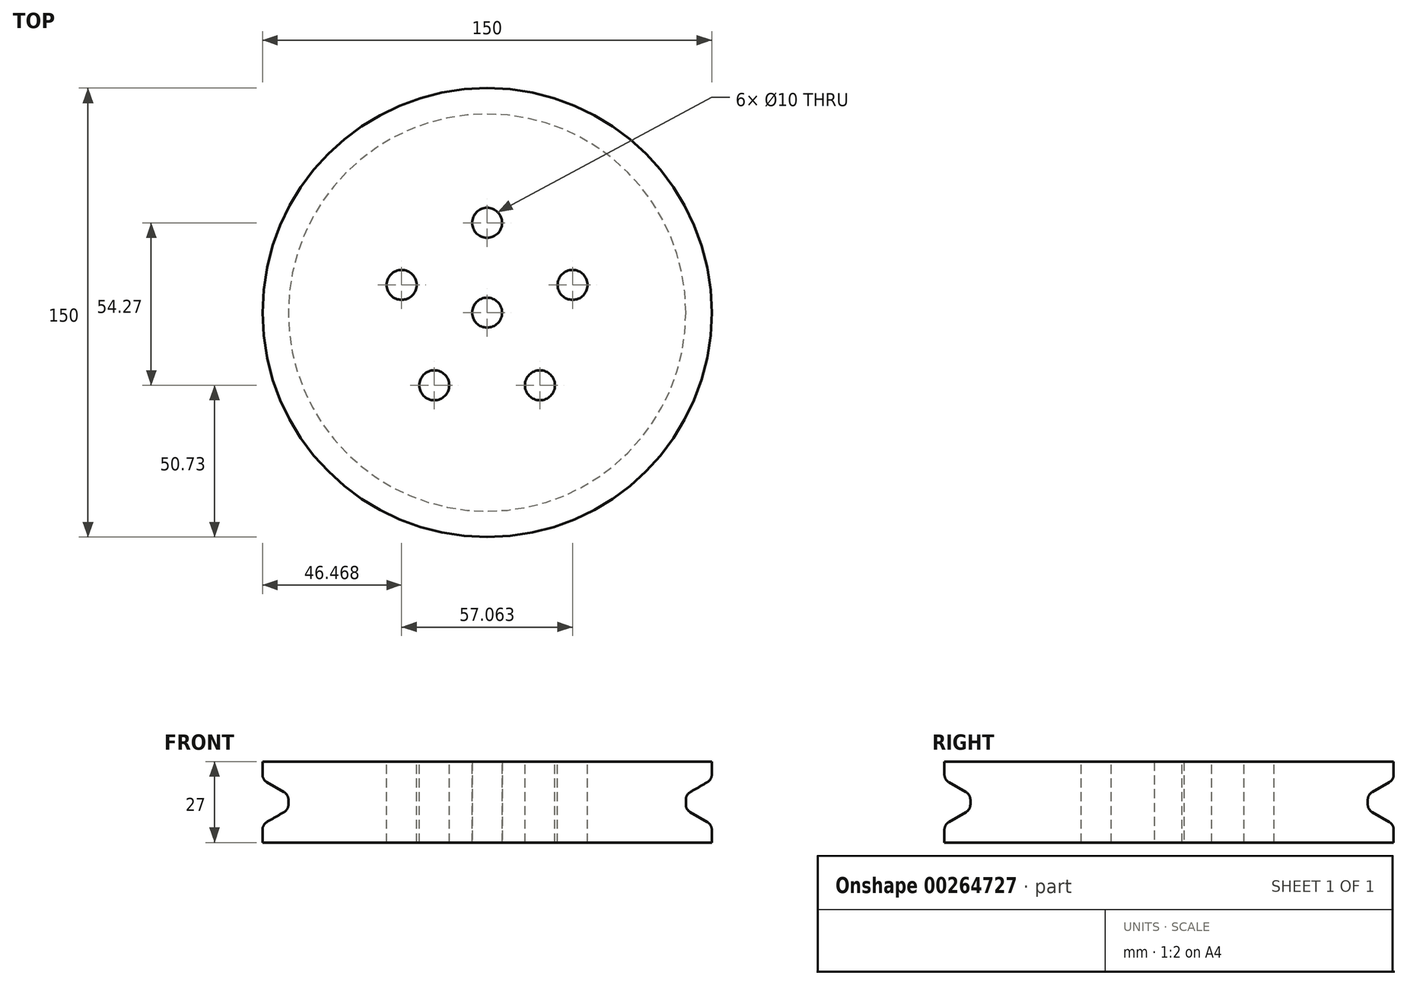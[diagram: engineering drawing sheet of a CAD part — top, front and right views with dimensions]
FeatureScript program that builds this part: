
annotation { "Feature Type Name" : "Feature", "Feature Type Description" : "" }
export const myFeature = defineFeature(function(context is Context, id is Id, definition is map)
    precondition{}
    {
        {
            var Q0;
            Q0=qCreatedBy(makeId("Right.planeOp"),FACE);
            var sketch = newSketch(context, id + "F0", { "sketchPlane" : qUnion([Q0])});
            skLineSegment(sketch, "E0", {"start": v(0, 20.55) * mm, "end": v(0, -14.5) * mm, "construction": true});
            skLineSegment(sketch, "E1", {"start": v(-5, 12.33) * mm, "end": v(-75, 12.33) * mm});
            skLineSegment(sketch, "E2", {"start": v(-75, 12.33) * mm, "end": v(-75, 6.33) * mm});
            skLineSegment(sketch, "E3", {"start": v(-75, 6.33) * mm, "end": v(-66.34, 1.33) * mm});
            skLineSegment(sketch, "E4", {"start": v(-66.34, 1.33) * mm, "end": v(-66.34, -3.67) * mm});
            skLineSegment(sketch, "E5", {"start": v(-66.34, -3.67) * mm, "end": v(-75, -8.67) * mm});
            skLineSegment(sketch, "E6", {"start": v(-75, -8.67) * mm, "end": v(-75, -14.67) * mm});
            skLineSegment(sketch, "E7", {"start": v(-75, -14.67) * mm, "end": v(-5, -14.67) * mm});
            skLineSegment(sketch, "E8", {"start": v(-5, -14.67) * mm, "end": v(-5, 12.33) * mm});
            skSolve(sketch);
        }
        {
            var Q0;
            Q0=makeQuery(id+"F0.imprint","IMPRINT",FACE,{"disambiguationData":[TD([[makeQuery(id+"F0.imprint","IMPRINT",EDGE,{"derivedFrom":sQuery(id+"F0.wireOp",EDGE,"E1")}),1.0]])]});
            var Q1;
            Q1=sQuery(id+"F0.wireOp",EDGE,"E0");
            revolve(context, id + "F1", {"entities" : qUnion([Q0]), "axis" : qUnion([Q1]), "revolveType" : RevolveType.FULL, "oppositeDirection" : true});
        }
        {
            var Q0;
            Q0=makeQuery(id+"F1.opRevolve","SWEPT_FACE",FACE,{"disambiguationData":[OSD([sQuery(id+"F0.wireOp",EDGE,"E1")])]});
            var sketch = newSketch(context, id + "F2", { "sketchPlane" : qUnion([Q0])});
            skCircle(sketch, "E9", {"center": v(0, 30) * mm, "radius": 5 * mm});
            skCircle(sketch, "E10.1.0", {"center": v(-28.53, 9.27) * mm, "radius": 5 * mm});
            skCircle(sketch, "E10.2.0", {"center": v(-17.63, -24.27) * mm, "radius": 5 * mm});
            skCircle(sketch, "E10.3.0", {"center": v(17.63, -24.27) * mm, "radius": 5 * mm});
            skCircle(sketch, "E10.4.0", {"center": v(28.53, 9.27) * mm, "radius": 5 * mm});
            skPoint(sketch, "E10.center", {"position": v(0, 0) * mm});
            skSolve(sketch);
        }
        {
            var Q0;
            Q0=makeQuery(id+"F2.imprint","IMPRINT",FACE,{"disambiguationData":[TD([[makeQuery(id+"F2.imprint","IMPRINT",EDGE,{"derivedFrom":sQuery(id+"F2.wireOp",EDGE,"E10.1.0")}),1.0]])]});
            var Q1;
            Q1=makeQuery(id+"F2.imprint","IMPRINT",FACE,{"disambiguationData":[TD([[makeQuery(id+"F2.imprint","IMPRINT",EDGE,{"derivedFrom":sQuery(id+"F2.wireOp",EDGE,"E9")}),1.0]])]});
            var Q2;
            Q2=makeQuery(id+"F2.imprint","IMPRINT",FACE,{"disambiguationData":[TD([[makeQuery(id+"F2.imprint","IMPRINT",EDGE,{"derivedFrom":sQuery(id+"F2.wireOp",EDGE,"E10.3.0")}),1.0]])]});
            var Q3;
            Q3=makeQuery(id+"F2.imprint","IMPRINT",FACE,{"disambiguationData":[TD([[makeQuery(id+"F2.imprint","IMPRINT",EDGE,{"derivedFrom":sQuery(id+"F2.wireOp",EDGE,"E10.2.0")}),1.0]])]});
            var Q4;
            Q4=makeQuery(id+"F2.imprint","IMPRINT",FACE,{"disambiguationData":[TD([[makeQuery(id+"F2.imprint","IMPRINT",EDGE,{"derivedFrom":sQuery(id+"F2.wireOp",EDGE,"E10.4.0")}),1.0]])]});
            extrude(context, id + "F3", {"entities" : qUnion([Q0, Q1, Q2, Q3, Q4]), "operationType" : NewBodyOperationType.REMOVE, "endBound" : BoundingType.UP_TO_NEXT, "oppositeDirection" : true, "depth" : 25 * mm});
        }
        {
            var Q0;
            Q0=makeQuery(id+"F1.opRevolve","SWEPT_EDGE",EDGE,{"disambiguationData":[OSD([sQuery(id+"F0.wireOp",EDGE,"E2"),sQuery(id+"F0.wireOp",EDGE,"E3")])]});
            var Q1;
            Q1=makeQuery(id+"F1.opRevolve","SWEPT_EDGE",EDGE,{"disambiguationData":[OSD([sQuery(id+"F0.wireOp",EDGE,"E3"),sQuery(id+"F0.wireOp",EDGE,"E4")])]});
            var Q2;
            Q2=makeQuery(id+"F1.opRevolve","SWEPT_EDGE",EDGE,{"disambiguationData":[OSD([sQuery(id+"F0.wireOp",EDGE,"E4"),sQuery(id+"F0.wireOp",EDGE,"E5")])]});
            var Q3;
            Q3=makeQuery(id+"F1.opRevolve","SWEPT_EDGE",EDGE,{"disambiguationData":[OSD([sQuery(id+"F0.wireOp",EDGE,"E5"),sQuery(id+"F0.wireOp",EDGE,"E6")])]});
            fillet(context, id + "F4", {"entities" : qUnion([Q0, Q1, Q2, Q3]), "radius" : 3 * mm, "tangentPropagation" : true, "allowEdgeOverflow" : false});
        }
    });
